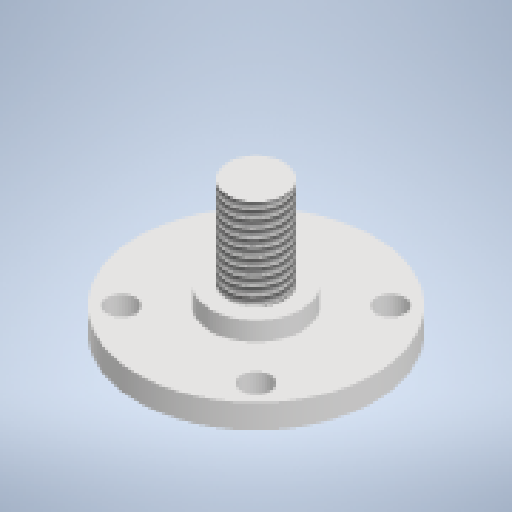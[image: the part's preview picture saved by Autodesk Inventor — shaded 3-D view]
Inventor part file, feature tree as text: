
AUTODESK INVENTOR PART (.ipt)
format: ipt  version: 2023.1 (Build 271208000, 208)  size: 265,216 bytes
history: native  units: mm
features: sketch x4, extrude x3, hole x1, thread x1
ambient origin geometry x8: Origin, YZ Plane, XZ Plane, XY Plane, X Axis, Y Axis, Z Axis, Center Point
bodies: Solid1 (feature_tree)
feature tree (9):
  extrude  "Extrusion1"  Depth=5.0mm TaperAngle=0.0deg
  hole  "Hole1"  [1 undecoded]
  extrude  "Extrusion2"  Depth=19.0mm
  extrude  "Extrusion3"  Depth=4.0mm TaperAngle=0.0deg
  thread  "Thread1"  [1 undecoded]
  sketch  "Sketch1"  dims[d0=50.0mm d1=5.0mm d2=0.0mm]
  sketch  "Sketch2"  dims[d3=20.0mm d4=135.0deg]
  sketch  "Sketch3"  dims[d5=40.0mm d7=360.0deg]
  sketch  "Sketch4"  dims[d9=6.0mm d10=6.0mm d11=4.0mm d12=2.0mm d13=90.0deg d14=8.0mm d15=20.594885mm d16=19.0mm d17=4.0mm d18=0.0mm d19=12.0mm d20=19.0mm d21=0.0mm d22=19.0mm d23=0.0mm]
note: 2 required parameter values undecoded (feature->parameter linkage not recoverable at this tier; creation-order binding heuristic only, values carry confidence <= 0.55)
